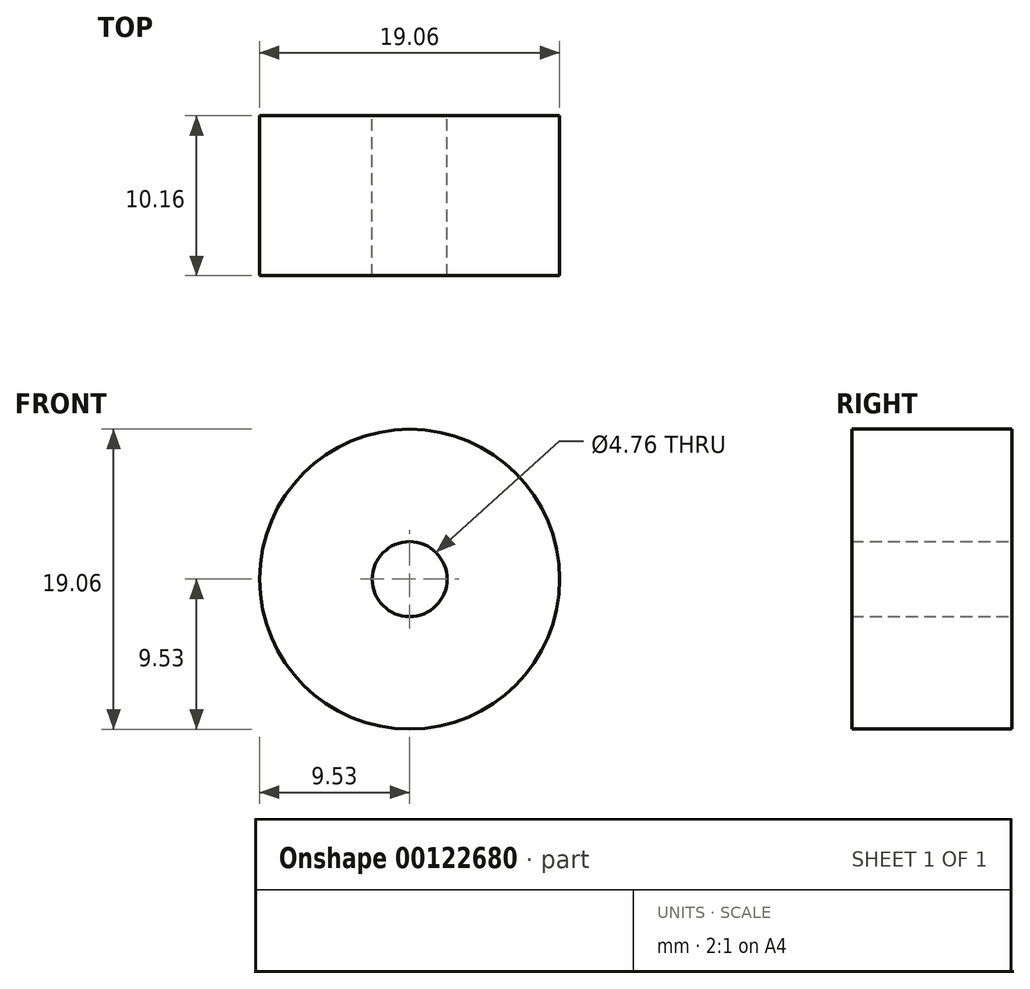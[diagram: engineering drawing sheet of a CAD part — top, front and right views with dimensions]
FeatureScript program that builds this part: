
annotation { "Feature Type Name" : "Feature", "Feature Type Description" : "" }
export const myFeature = defineFeature(function(context is Context, id is Id, definition is map)
    precondition{}
    {
        {
            var Q0;
            Q0=qCreatedBy(makeId("Front.planeOp"),FACE);
            var sketch = newSketch(context, id + "F0", { "sketchPlane" : qUnion([Q0])});
            skCircle(sketch, "E0", {"center": v(0, 0) * mm, "radius": 9.53 * mm});
            skCircle(sketch, "E1", {"center": v(0, 0) * mm, "radius": 2.38 * mm});
            skSolve(sketch);
        }
        {
            var Q0;
            Q0=makeQuery(id+"F0.imprint","IMPRINT",FACE,{"disambiguationData":[TD([[makeQuery(id+"F0.imprint","IMPRINT",EDGE,{"derivedFrom":sQuery(id+"F0.wireOp",EDGE,"E0")}),1.0]])]});
            extrude(context, id + "F1", {"entities" : qUnion([Q0]), "depth" : 10.16 * mm});
        }
    });
